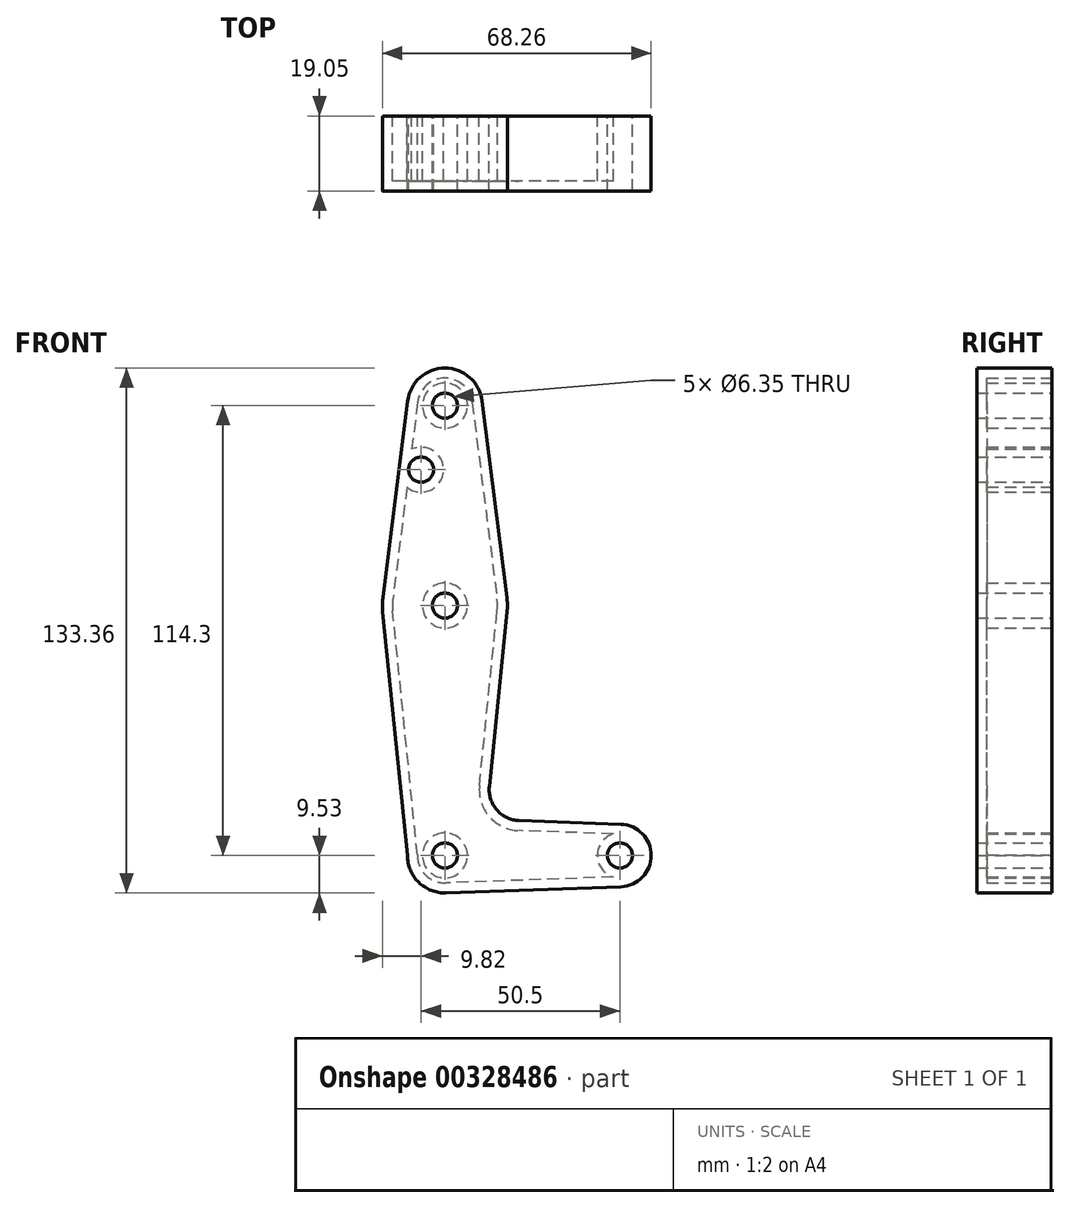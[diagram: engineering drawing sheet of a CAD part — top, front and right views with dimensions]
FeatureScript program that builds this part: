
annotation { "Feature Type Name" : "Feature", "Feature Type Description" : "" }
export const myFeature = defineFeature(function(context is Context, id is Id, definition is map)
    precondition{}
    {
        {
            var Q0;
            Q0=qCreatedBy(makeId("Front.planeOp"),FACE);
            var sketch = newSketch(context, id + "F0", { "sketchPlane" : qUnion([Q0])});
            skLineSegment(sketch, "E0", {"start": v(0, 0) * mm, "end": v(0, 114.3) * mm, "construction": true});
            skLineSegment(sketch, "E1", {"start": v(0, 0) * mm, "end": v(44.45, 0) * mm, "construction": true});
            skCircle(sketch, "E2", {"center": v(44.45, 0) * mm, "radius": 7.94 * mm});
            skCircle(sketch, "E3", {"center": v(0, 0) * mm, "radius": 9.53 * mm});
            skCircle(sketch, "E4", {"center": v(0, 63.5) * mm, "radius": 15.88 * mm});
            skCircle(sketch, "E5", {"center": v(0, 114.3) * mm, "radius": 9.53 * mm});
            skLineSegment(sketch, "E6", {"start": v(9.45, 115.5) * mm, "end": v(15.75, 65.48) * mm});
            skLineSegment(sketch, "E7", {"start": v(-9.52, 0) * mm, "end": v(-15.8, 61.9) * mm});
            skLineSegment(sketch, "E8", {"start": v(44.73, -7.93) * mm, "end": v(0.34, -9.52) * mm});
            skCircle(sketch, "E9", {"center": v(0, 114.3) * mm, "radius": 3.18 * mm});
            skCircle(sketch, "E10", {"center": v(0, 63.5) * mm, "radius": 3.18 * mm});
            skCircle(sketch, "E11", {"center": v(0, 0) * mm, "radius": 3.18 * mm});
            skCircle(sketch, "E12", {"center": v(44.45, 0) * mm, "radius": 3.18 * mm});
            skCircle(sketch, "E13", {"center": v(-6.05, 98.02) * mm, "radius": 3.18 * mm});
            skLineSegment(sketch, "E14.MirrorCS", {"start": v(-9.45, 115.5) * mm, "end": v(-15.75, 65.48) * mm});
            skLineSegment(sketch, "E15.MirrorCS", {"start": v(44.73, 7.93) * mm, "end": v(18.85, 8.86) * mm});
            skLineSegment(sketch, "E16.MirrorCS", {"start": v(11.3, 17.52) * mm, "end": v(15.8, 61.9) * mm});
            skPoint(sketch, "E17.newPointA", {"position": v(9.52, 0) * mm});
            skPoint(sketch, "E17.newPointB", {"position": v(0.34, 9.52) * mm});
            skArc(sketch, "E17.filletArc", {"start": v(11.3, 17.52) * mm, "mid": v(13.2, 11.55) * mm, "end": v(18.85, 8.86) * mm});
            skSolve(sketch);
        }
        {
            var Q0;
            Q0 = qSketchRegion(id + "F0", true);
            extrude(context, id + "F1", {"entities" : qUnion([Q0]), "depth" : 19.05 * mm});
        }
        {
            var Q0;
            Q0=makeQuery(id+"F1.opExtrude","CAP_FACE",FACE,{"disambiguationData":[OSD([sQuery(id+"F0.wireOp",EDGE,"E2"),sQuery(id+"F0.wireOp",EDGE,"E3"),sQuery(id+"F0.wireOp",EDGE,"E4"),sQuery(id+"F0.wireOp",EDGE,"E5"),sQuery(id+"F0.wireOp",EDGE,"E6"),sQuery(id+"F0.wireOp",EDGE,"E7"),sQuery(id+"F0.wireOp",EDGE,"E8"),sQuery(id+"F0.wireOp",EDGE,"E9"),sQuery(id+"F0.wireOp",EDGE,"E10"),sQuery(id+"F0.wireOp",EDGE,"E11"),sQuery(id+"F0.wireOp",EDGE,"E12"),sQuery(id+"F0.wireOp",EDGE,"E13"),sQuery(id+"F0.wireOp",EDGE,"E14.MirrorCS"),sQuery(id+"F0.wireOp",EDGE,"E15.MirrorCS"),sQuery(id+"F0.wireOp",EDGE,"E16.MirrorCS"),sQuery(id+"F0.wireOp",EDGE,"E17.filletArc")])],"isStart":true});
            shell(context, id + "F2", {"entities" : qUnion([Q0]), "thickness" : 2.54 * mm});
        }
    });
